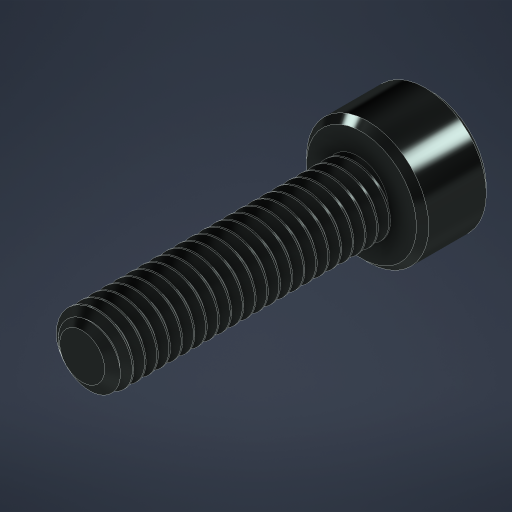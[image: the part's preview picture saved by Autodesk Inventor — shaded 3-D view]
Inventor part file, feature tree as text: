
AUTODESK INVENTOR PART (.ipt)
format: ipt  version: 2024 (Build 280153000, 153)  size: 888,320 bytes
history: native  units: in
note: dims shown in document units (in); Inventor stores cm internally (conversion verified against a paired STEP export)
features: chamfer x1
ambient origin geometry x8: Origin, YZ Plane, XZ Plane, XY Plane, X Axis, Y Axis, Z Axis, Center Point
bodies: Solid1 (feature_tree)
feature tree (1):
  chamfer  "Chamfer1"  [1 undecoded]
note: 1 required parameter value undecoded (feature->parameter linkage not recoverable at this tier; creation-order binding heuristic only, values carry confidence <= 0.55)
